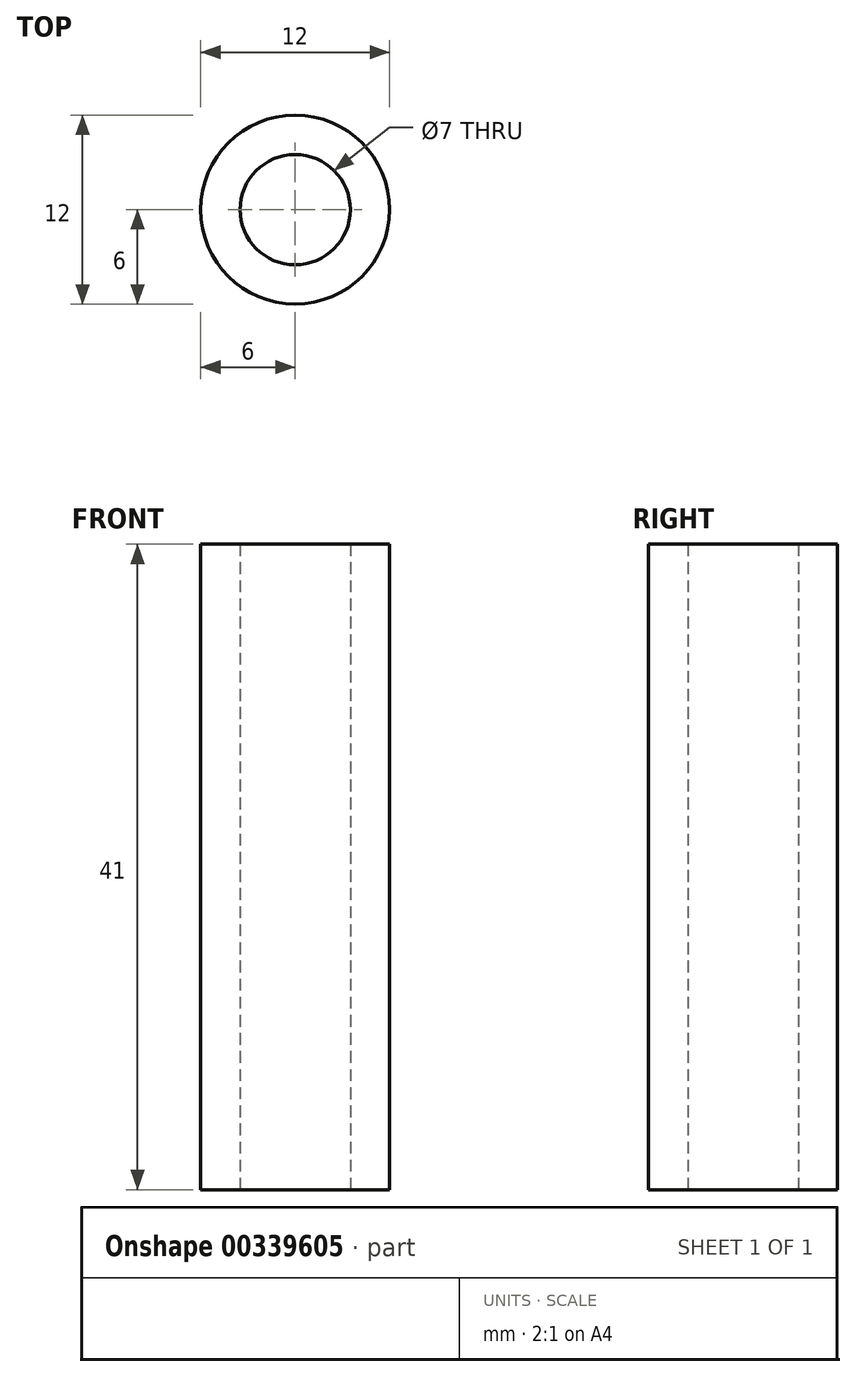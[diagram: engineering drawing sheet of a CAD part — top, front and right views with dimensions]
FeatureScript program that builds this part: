
annotation { "Feature Type Name" : "Feature", "Feature Type Description" : "" }
export const myFeature = defineFeature(function(context is Context, id is Id, definition is map)
    precondition{}
    {
        {
            var Q0;
            Q0=qCreatedBy(makeId("Top.planeOp"),FACE);
            var sketch = newSketch(context, id + "F0", { "sketchPlane" : qUnion([Q0])});
            skCircle(sketch, "E0", {"center": v(0, 0) * mm, "radius": 3.5 * mm});
            skCircle(sketch, "E1", {"center": v(0, 0) * mm, "radius": 6 * mm});
            skSolve(sketch);
        }
        {
            var Q0;
            Q0=qSketchRegion(id+"F0",true);
            extrude(context, id + "F1", {"entities" : qUnion([Q0]), "depth" : 41 * mm});
        }
    });
